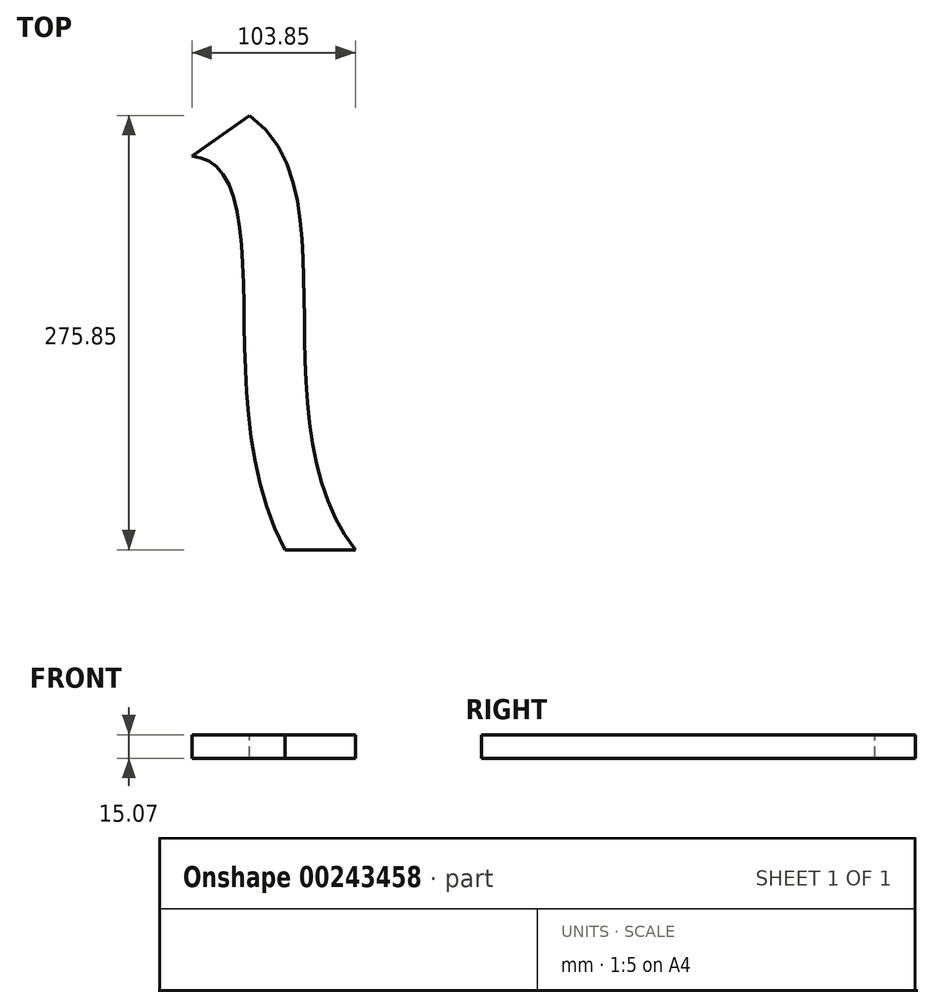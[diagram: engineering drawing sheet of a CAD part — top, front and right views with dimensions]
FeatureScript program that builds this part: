
annotation { "Feature Type Name" : "Feature", "Feature Type Description" : "" }
export const myFeature = defineFeature(function(context is Context, id is Id, definition is map)
    precondition{}
    {
        {
            var Q0;
            Q0=qCreatedBy(makeId("Front.planeOp"),FACE);
            var sketch = newSketch(context, id + "F0", { "sketchPlane" : qUnion([Q0])});
            skLineSegment(sketch, "E0.bottom", {"start": v(12.92, 0.36) * mm, "end": v(57.65, 0.36) * mm});
            skLineSegment(sketch, "E0.top", {"start": v(12.92, 15.43) * mm, "end": v(57.65, 15.43) * mm});
            skLineSegment(sketch, "E0.left", {"start": v(12.92, 0.36) * mm, "end": v(12.92, 15.43) * mm});
            skLineSegment(sketch, "E0.right", {"start": v(57.65, 0.36) * mm, "end": v(57.65, 15.43) * mm});
            skSolve(sketch);
        }
        {
            var Q0;
            Q0=qCreatedBy(makeId("Top.planeOp"),FACE);
            var sketch = newSketch(context, id + "F1", { "sketchPlane" : qUnion([Q0])});
            skFitSpline(sketch, "E1", {"points": [v(30.24, 0) * mm, v(-32.05, 260.05) * mm], "startDerivative": vector(-165.6, 273.04) * mm, "endDerivative": vector(-186.3, 81.24) * mm});
            skSolve(sketch);
        }
        {
            var Q0;
            Q0=makeQuery(id+"F0.imprint","IMPRINT",FACE,{"disambiguationData":[TD([[makeQuery(id+"F0.imprint","IMPRINT",EDGE,{"derivedFrom":sQuery(id+"F0.wireOp",EDGE,"E0.bottom")}),1.0]])]});
            var Q1;
            Q1=sQuery(id+"F1.wireOp",EDGE,"E1");
            sweep(context, id + "F2", {"profiles" : qUnion([Q0]), "path" : qUnion([Q1])});
        }
    });
